# Revit family: Sink-Topmount-Acorn-CDADA-3120-45,55_Series
name_source: partatom
category: Plumbing Fixtures
units: mm (PartAtom-declared; Revit-internal decimal feet)

## family parameters
Cut with Voids When Loaded = No
Host = Face
OmniClass Number = 23.45.05.14.14
OmniClass Title = Sinks/Lavatories
Part Type = Normal
Room Calculation Point = No
Round Connector Dimension = Use Diameter
Shared = Yes

## types (12) — shared parameters
ADA Compliant = Yes
Assembly Code = D2010440
Bottom Faucet Hole Distance = 4"
Bowl Length = 16"
Bowl Width = 22"
CW Connection = No
CWFU = 3
Compliance Certifications = ASME A112.19.3/CSA B45.4, IAPMO® Certified
Default Elevation = 34"
Description = Stainless Steel Drop In Sink
Drain Opening Size = 3 1/2"
Finish = Stainless Steel-Acorn-Satin
HW Connection = No
HWFU = 3
Installation Type = Wall Mounted
Length = 19 1/2"
Manufacturer = Acorn
Material = Stainless Steel-Acorn-Satin
Top Faucet Hole Distance = 4"
URL = https://www.acorneng.com
Vent Connection = No
WFU = 4
Waste Connection = No
Width = 31"

## per-type parameters (varying)
| type | -0 Blank, No Deck Punching | -1 Single Hole Centered | -2DL Single Hole Centered w/ Slotted Hole Left | -2DR Single Hole Centered w/ Slotted Hole Right | -4DL 3 Holes on 4 Centers w/ Slotted Hole Left | -4DR 3 Holes on 4 Centers w/ Slotted Hole Right | Height | Left Bottom Faucet Hole Depth | Left Central Faucet Hole Depth | Left Top Faucet Hole Depth | Right Bottom Faucet Hole Depth | Right Central Faucet Hole Depth | Right Top Faucet Hole Depth | Slotted Hole Left Depth | Slotted Hole Right Depth |
| CDADA-3120-55-0 | Yes | No | No | No | No | No | 5 1/2" | 1" | 1" | 1" | 1" | 1" | 1" | 1" | 1" |
| CDADA-3120-55-1 | No | Yes | No | No | No | No | 5 1/2" | 1" | 1" | 1" | 1" | 2" | 1" | 1" | 1" |
| CDADA-3120-55-2DL | No | No | Yes | No | No | No | 5 1/2" | 1" | 1" | 1" | 1" | 2" | 1" | 2" | 1" |
| CDADA-3120-55-2DR | No | No | No | Yes | No | No | 5 1/2" | 1" | 2" | 1" | 1" | 1" | 1" | 1" | 2" |
| CDADA-3120-55-4DL | No | No | No | No | Yes | No | 5 1/2" | 1" | 1" | 1" | 2" | 2" | 2" | 2" | 1" |
| CDADA-3120-55-4DR | No | No | No | No | No | Yes | 5 1/2" | 2" | 2" | 2" | 1" | 1" | 1" | 1" | 2" |
| CDADA-3120-45-0 | Yes | No | No | No | No | No | 4 1/2" | 1" | 1" | 1" | 1" | 1" | 1" | 1" | 1" |
| CDADA-3120-45-1 | No | Yes | No | No | No | No | 4 1/2" | 1" | 2" | 1" | 1" | 1" | 1" | 1" | 1" |
| CDADA-3120-45-2DL | No | No | Yes | No | No | No | 4 1/2" | 1" | 1" | 1" | 1" | 2" | 1" | 2" | 1" |
| CDADA-3120-45-2DR | No | No | No | Yes | No | No | 4 1/2" | 1" | 2" | 1" | 1" | 1" | 1" | 1" | 2" |
| CDADA-3120-45-4DL | No | No | No | No | Yes | No | 4 1/2" | 1" | 1" | 1" | 2" | 2" | 2" | 2" | 1" |
| CDADA-3120-45-4DR | No | No | No | No | No | Yes | 4 1/2" | 2" | 2" | 2" | 1" | 1" | 1" | 1" | 2" |

note: column(s) folded — value = type name in every type: Model

## geometry (parser evidence)
native form markers: Sweep x3
no freeform markers — native parametric forms only
